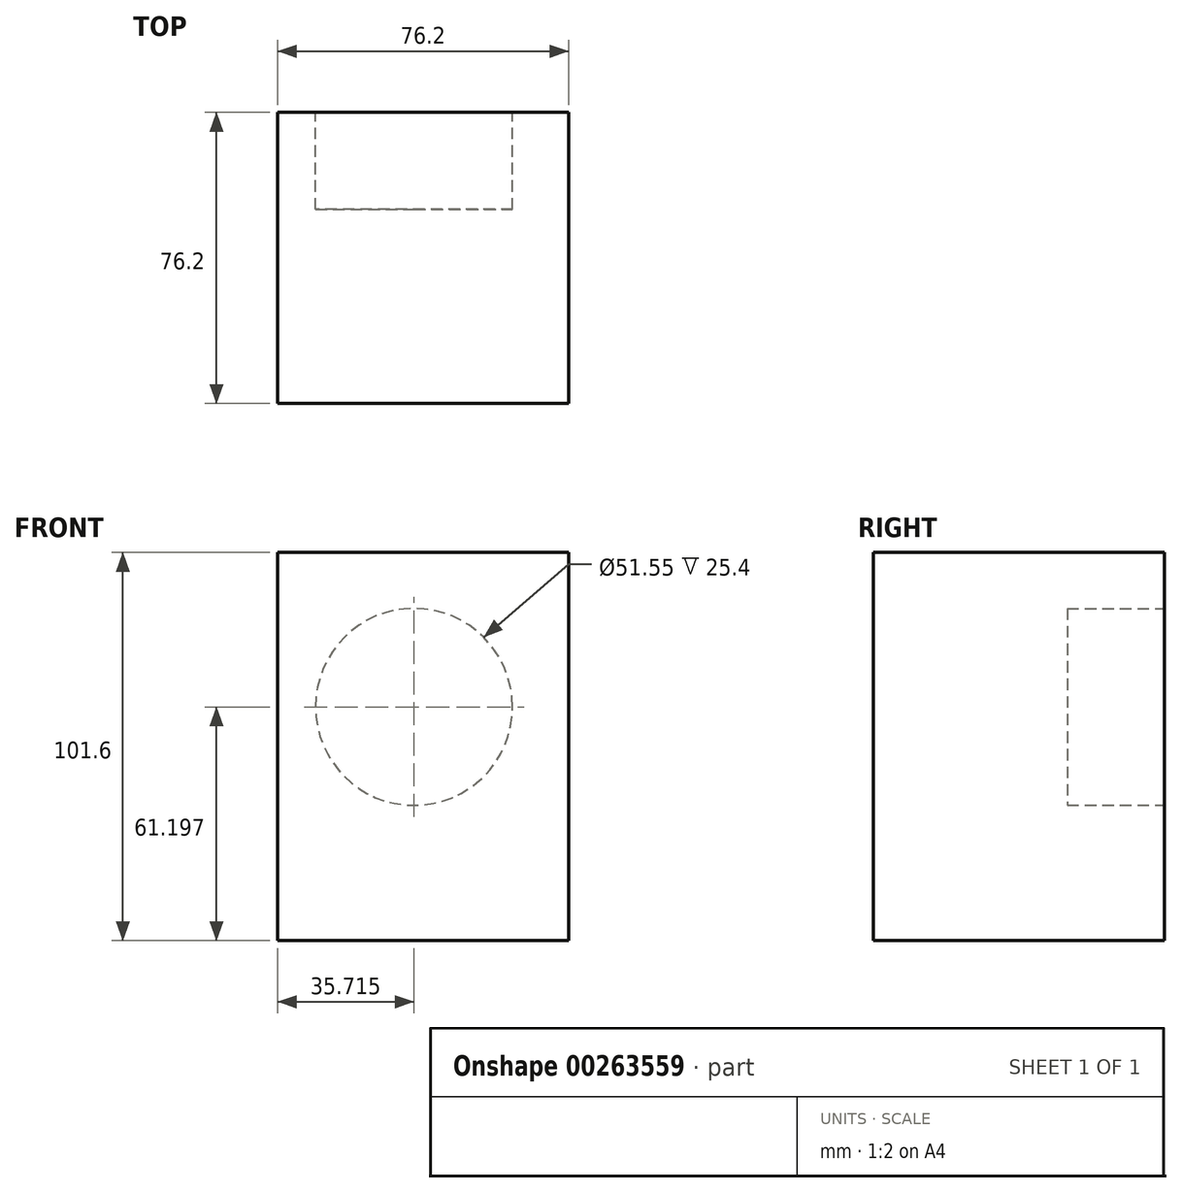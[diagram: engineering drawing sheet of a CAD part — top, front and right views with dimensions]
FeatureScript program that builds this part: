
annotation { "Feature Type Name" : "Feature", "Feature Type Description" : "" }
export const myFeature = defineFeature(function(context is Context, id is Id, definition is map)
    precondition{}
    {
        {
            var Q0;
            Q0=qCreatedBy(makeId("Front.planeOp"),FACE);
            var sketch = newSketch(context, id + "F0", { "sketchPlane" : qUnion([Q0])});
            skLineSegment(sketch, "E0.bottom", {"start": v(0, 0) * mm, "end": v(76.2, 0) * mm});
            skLineSegment(sketch, "E0.top", {"start": v(0, 101.6) * mm, "end": v(76.2, 101.6) * mm});
            skLineSegment(sketch, "E0.left", {"start": v(0, 0) * mm, "end": v(0, 101.6) * mm});
            skLineSegment(sketch, "E0.right", {"start": v(76.2, 0) * mm, "end": v(76.2, 101.6) * mm});
            skSolve(sketch);
        }
        {
            var Q0;
            Q0=makeQuery(id+"F0.imprint","IMPRINT",FACE,{"disambiguationData":[TD([[makeQuery(id+"F0.imprint","IMPRINT",EDGE,{"derivedFrom":sQuery(id+"F0.wireOp",EDGE,"E0.bottom")}),1.0]])]});
            extrude(context, id + "F1", {"entities" : qUnion([Q0]), "oppositeDirection" : true, "depth" : 76.2 * mm});
        }
        {
            var Q0;
            Q0=makeQuery(id+"F1.opExtrude","CAP_FACE",FACE,{"disambiguationData":[OSD([sQuery(id+"F0.wireOp",EDGE,"E0.bottom"),sQuery(id+"F0.wireOp",EDGE,"E0.top"),sQuery(id+"F0.wireOp",EDGE,"E0.left"),sQuery(id+"F0.wireOp",EDGE,"E0.right")])],"isStart":false});
            var sketch = newSketch(context, id + "F2", { "sketchPlane" : qUnion([Q0])});
            skCircle(sketch, "E1", {"center": v(-35.72, 61.2) * mm, "radius": 25.78 * mm});
            skSolve(sketch);
        }
        {
            var Q0;
            Q0=makeQuery(id+"F2.imprint","IMPRINT",FACE,{"disambiguationData":[TD([[makeQuery(id+"F2.imprint","IMPRINT",EDGE,{"derivedFrom":sQuery(id+"F2.wireOp",EDGE,"E1")}),1.0]])]});
            extrude(context, id + "F3", {"entities" : qUnion([Q0]), "operationType" : NewBodyOperationType.REMOVE, "oppositeDirection" : true, "depth" : 25.4 * mm});
        }
    });
